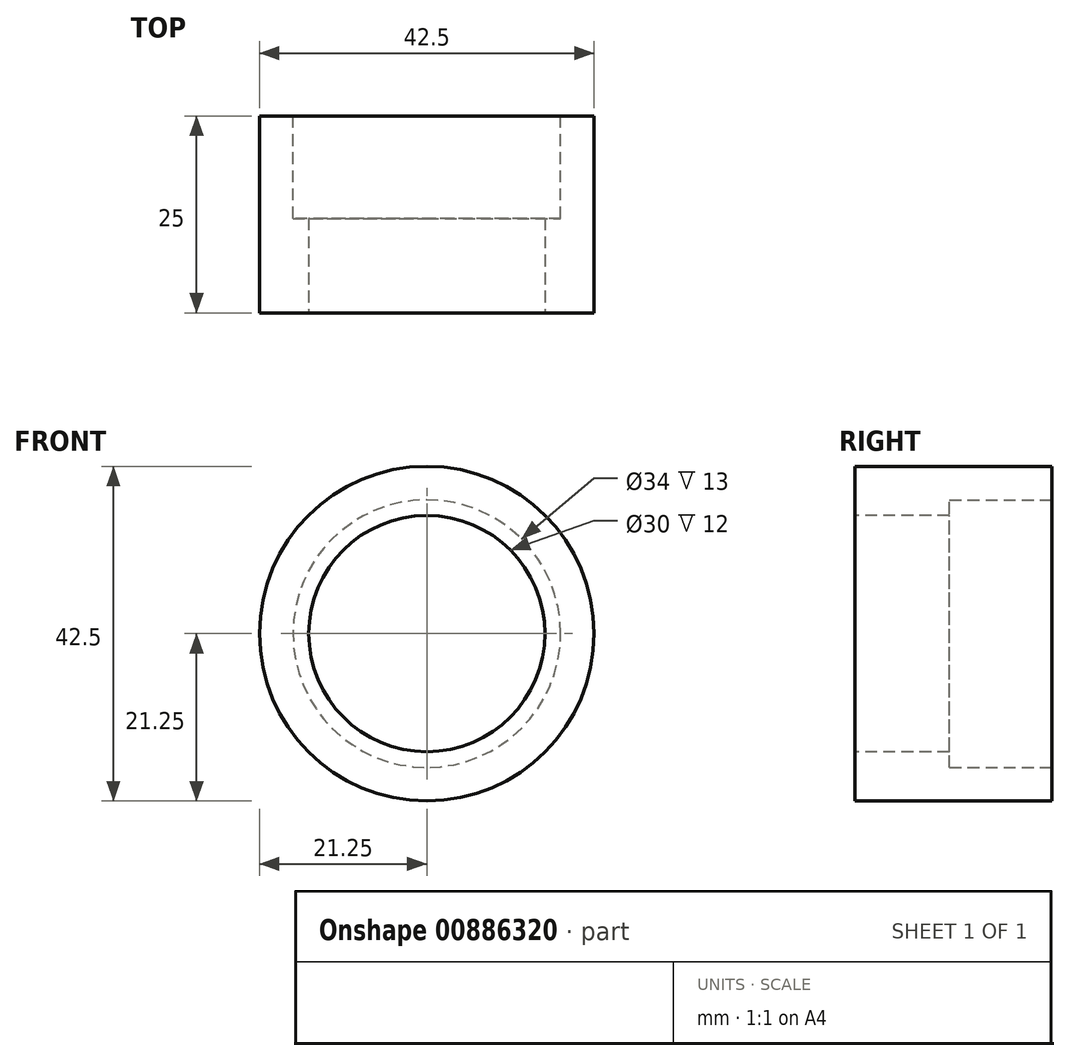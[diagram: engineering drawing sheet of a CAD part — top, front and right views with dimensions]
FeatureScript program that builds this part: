
annotation { "Feature Type Name" : "Feature", "Feature Type Description" : "" }
export const myFeature = defineFeature(function(context is Context, id is Id, definition is map)
    precondition{}
    {
        {
            var Q0;
            Q0=qCreatedBy(makeId("Front.planeOp"),FACE);
            var sketch = newSketch(context, id + "F0", { "sketchPlane" : qUnion([Q0])});
            skCircle(sketch, "E0", {"center": v(0, 0) * mm, "radius": 17 * mm});
            skCircle(sketch, "E1", {"center": v(0, 0) * mm, "radius": 15 * mm});
            skCircle(sketch, "E2", {"center": v(0, 0) * mm, "radius": 21.25 * mm});
            skSolve(sketch);
        }
        {
            var Q0;
            Q0=makeQuery(id+"F0.imprint","IMPRINT",FACE,{"disambiguationData":[TD([[makeQuery(id+"F0.imprint","IMPRINT",EDGE,{"derivedFrom":sQuery(id+"F0.wireOp",EDGE,"E0")}),-1.0]])]});
            extrude(context, id + "F1", {"entities" : qUnion([Q0]), "depth" : 25 * mm, "offsetDistance" : 25 * mm});
        }
        {
            var Q0;
            Q0=makeQuery(id+"F1.opExtrude","CAP_FACE",FACE,{"disambiguationData":[OSD([sQuery(id+"F0.wireOp",EDGE,"E0"),sQuery(id+"F0.wireOp",EDGE,"E2")])],"isStart":false});
            var sketch = newSketch(context, id + "F2", { "sketchPlane" : qUnion([Q0])});
            skCircle(sketch, "E3", {"center": v(0, 0) * mm, "radius": 15 * mm});
            skSolve(sketch);
        }
        {
            var Q0;
            Q0=makeQuery(id+"F2.imprint","IMPRINT",FACE,{"disambiguationData":[TD([[makeQuery(id+"F2.imprint","IMPRINT",EDGE,{"derivedFrom":sQuery(id+"F2.wireOp",EDGE,"E3")}),-1.0]])]});
            extrude(context, id + "F3", {"entities" : qUnion([Q0]), "operationType" : NewBodyOperationType.ADD, "oppositeDirection" : true, "depth" : 12 * mm, "offsetDistance" : 25 * mm});
        }
    });
